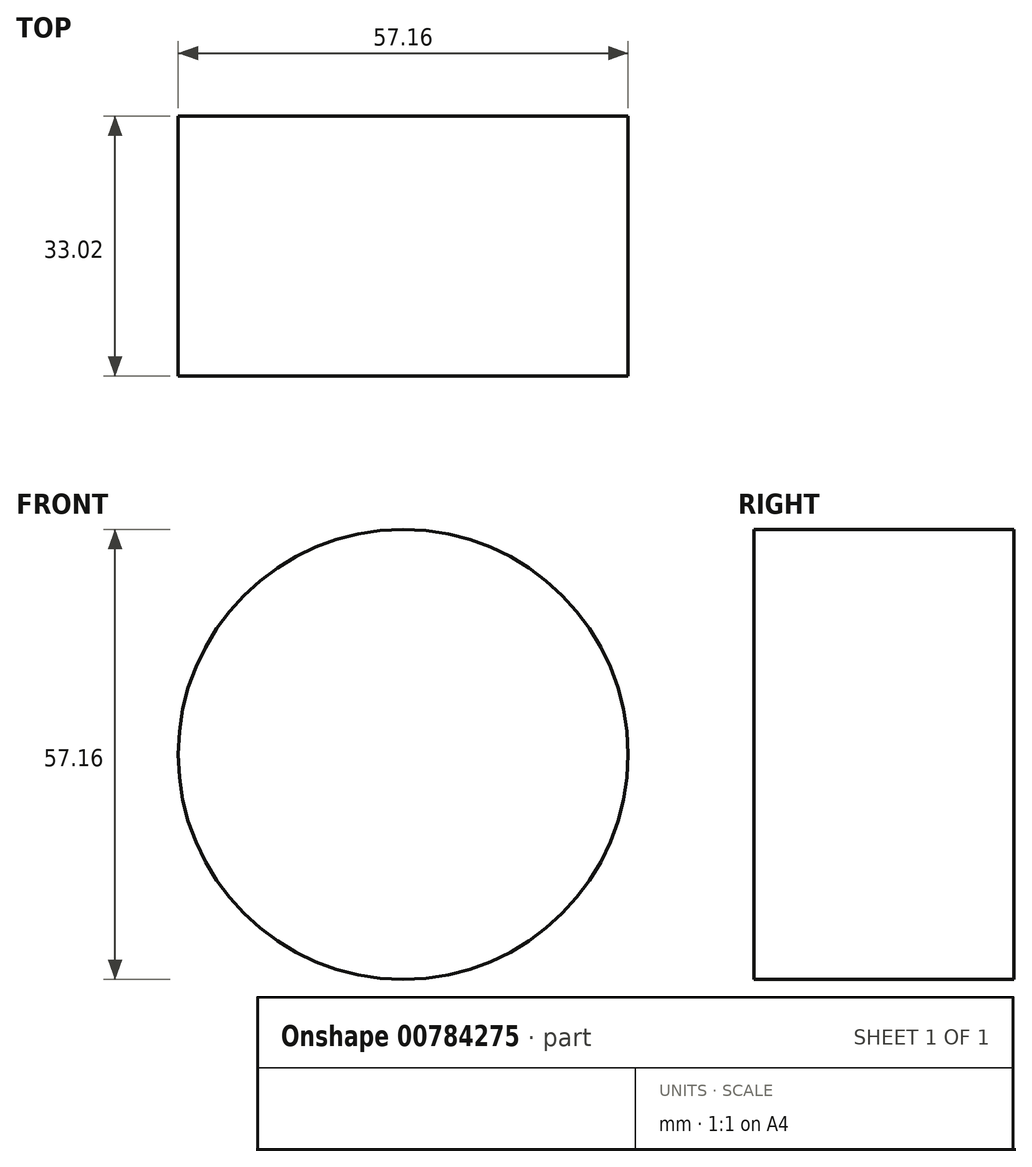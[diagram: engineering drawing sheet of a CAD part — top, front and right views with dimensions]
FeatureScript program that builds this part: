
annotation { "Feature Type Name" : "Feature", "Feature Type Description" : "" }
export const myFeature = defineFeature(function(context is Context, id is Id, definition is map)
    precondition{}
    {
        {
            var Q0;
            Q0=qCreatedBy(makeId("Front.planeOp"),FACE);
            var sketch = newSketch(context, id + "F0", { "sketchPlane" : qUnion([Q0])});
            skCircle(sketch, "E0", {"center": v(0, 0) * mm, "radius": 28.58 * mm});
            skSolve(sketch);
        }
        {
            var Q0;
            Q0 = qSketchRegion(id + "F0", true);
            extrude(context, id + "F1", {"entities" : qUnion([Q0]), "depth" : 33.02 * mm, "offsetDistance" : 25.4 * mm, "symmetric" : true});
        }
    });
